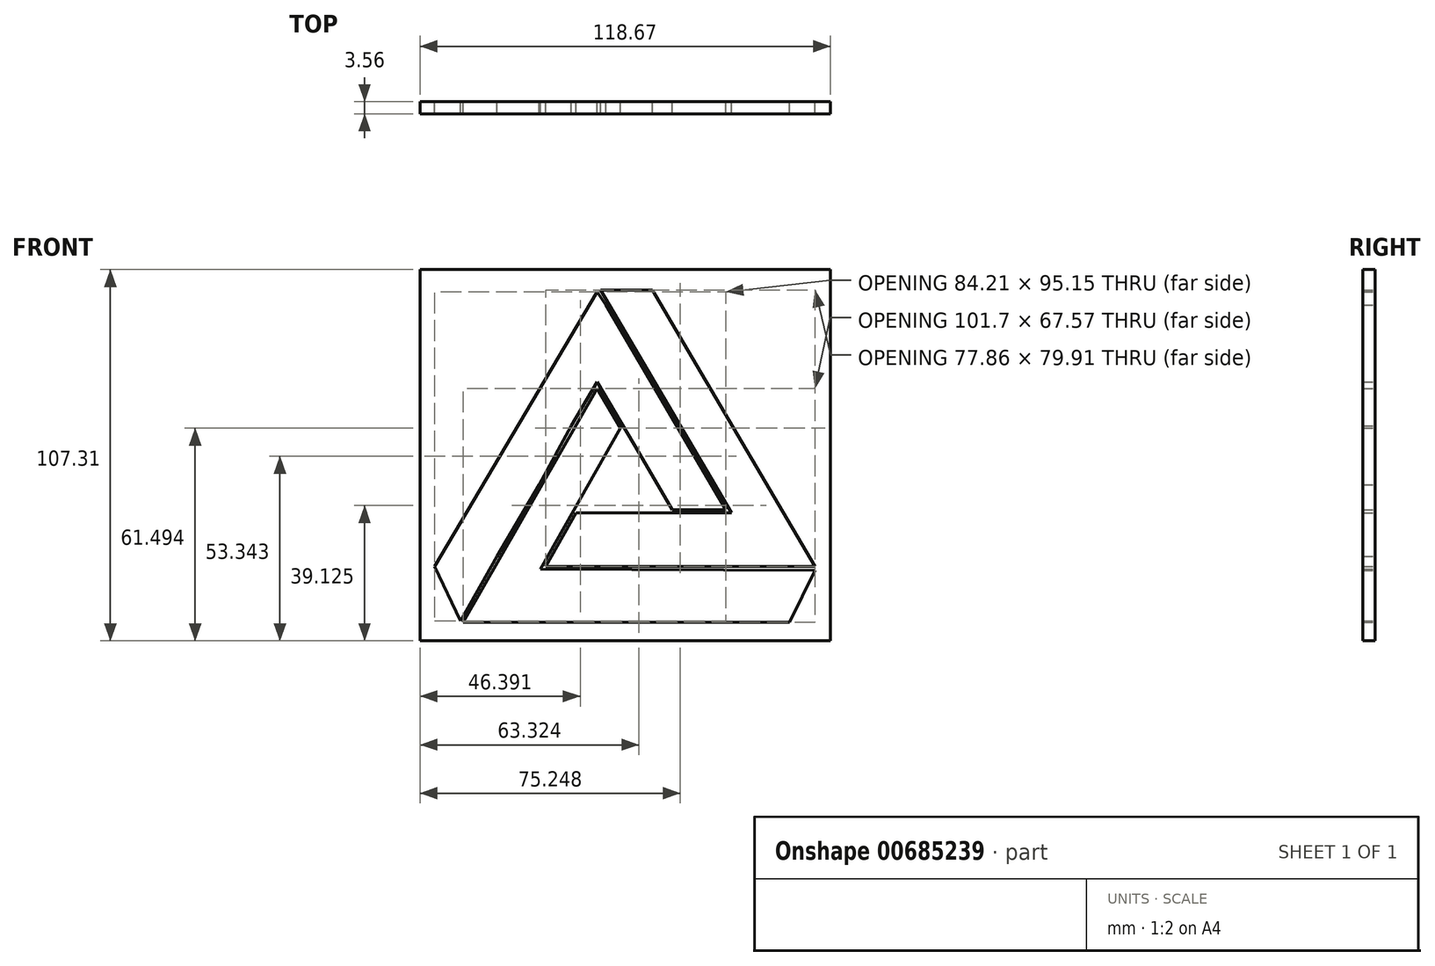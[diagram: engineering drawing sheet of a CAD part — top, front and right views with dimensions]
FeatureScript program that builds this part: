
annotation { "Feature Type Name" : "Feature", "Feature Type Description" : "" }
export const myFeature = defineFeature(function(context is Context, id is Id, definition is map)
    precondition{}
    {
        {
            var Q0;
            Q0=qCreatedBy(makeId("Front.planeOp"),FACE);
            var sketch = newSketch(context, id + "F0", { "sketchPlane" : qUnion([Q0])});
            skLineSegment(sketch, "E0", {"start": v(-4.74, 43.06) * mm, "end": v(10.26, 43.06) * mm});
            skLineSegment(sketch, "E1", {"start": v(10.26, 43.06) * mm, "end": v(19.28, 27.66) * mm});
            skLineSegment(sketch, "E2", {"start": v(19.28, 27.66) * mm, "end": v(57.2, -36.85) * mm});
            skLineSegment(sketch, "E3", {"start": v(57.2, -36.85) * mm, "end": v(22.98, -36.85) * mm});
            skLineSegment(sketch, "E4", {"start": v(22.98, -36.85) * mm, "end": v(-20.65, -36.85) * mm});
            skLineSegment(sketch, "E5", {"start": v(-20.65, -36.85) * mm, "end": v(-11.9, -21.44) * mm});
            skLineSegment(sketch, "E6", {"start": v(-11.9, -21.44) * mm, "end": v(33.16, -21.44) * mm});
            skLineSegment(sketch, "E7", {"start": v(33.16, -21.44) * mm, "end": v(-4.74, 43.06) * mm});
            skLineSegment(sketch, "E8", {"start": v(-5.76, 42.53) * mm, "end": v(-26.28, 7.81) * mm});
            skLineSegment(sketch, "E9", {"start": v(-26.28, 7.81) * mm, "end": v(-52.68, -36.85) * mm});
            skLineSegment(sketch, "E10", {"start": v(-52.68, -36.85) * mm, "end": v(-45.26, -52.62) * mm});
            skLineSegment(sketch, "E11", {"start": v(-45.26, -52.62) * mm, "end": v(-34.75, -33.95) * mm});
            skLineSegment(sketch, "E12", {"start": v(-34.75, -33.95) * mm, "end": v(-30.35, -26.51) * mm});
            skLineSegment(sketch, "E13", {"start": v(-30.35, -26.51) * mm, "end": v(-22.52, -13.27) * mm});
            skLineSegment(sketch, "E14", {"start": v(-22.52, -13.27) * mm, "end": v(-13.24, 3.73) * mm});
            skLineSegment(sketch, "E15", {"start": v(-13.24, 3.73) * mm, "end": v(-5.73, 16.44) * mm});
            skLineSegment(sketch, "E16", {"start": v(-5.73, 16.44) * mm, "end": v(6.53, -4.42) * mm});
            skLineSegment(sketch, "E17", {"start": v(6.53, -4.42) * mm, "end": v(15.97, -20.47) * mm});
            skLineSegment(sketch, "E18", {"start": v(15.97, -20.47) * mm, "end": v(31.52, -20.47) * mm});
            skLineSegment(sketch, "E19", {"start": v(31.52, -20.47) * mm, "end": v(23.42, -6.68) * mm});
            skLineSegment(sketch, "E20", {"start": v(23.42, -6.68) * mm, "end": v(16.9, 4.43) * mm});
            skLineSegment(sketch, "E21", {"start": v(16.9, 4.43) * mm, "end": v(12.07, 12.63) * mm});
            skLineSegment(sketch, "E22", {"start": v(12.07, 12.63) * mm, "end": v(5.95, 23.05) * mm});
            skLineSegment(sketch, "E23", {"start": v(5.95, 23.05) * mm, "end": v(-3.23, 38.67) * mm});
            skLineSegment(sketch, "E24", {"start": v(-3.23, 38.67) * mm, "end": v(-5.76, 42.53) * mm});
            skLineSegment(sketch, "E25", {"start": v(57.2, -37.99) * mm, "end": v(49.84, -53.05) * mm});
            skLineSegment(sketch, "E26", {"start": v(49.84, -53.05) * mm, "end": v(-44.5, -53.05) * mm});
            skLineSegment(sketch, "E27", {"start": v(-44.5, -53.05) * mm, "end": v(-5.76, 14.52) * mm});
            skLineSegment(sketch, "E28", {"start": v(-5.76, 14.52) * mm, "end": v(0.97, 3.08) * mm});
            skLineSegment(sketch, "E29", {"start": v(0.97, 3.08) * mm, "end": v(-22.15, -37.6) * mm});
            skLineSegment(sketch, "E30", {"start": v(-22.15, -37.6) * mm, "end": v(57.2, -37.99) * mm});
            skLineSegment(sketch, "E31.bottom", {"start": v(-56.97, 48.92) * mm, "end": v(61.7, 48.92) * mm});
            skLineSegment(sketch, "E31.top", {"start": v(-56.97, -58.39) * mm, "end": v(61.7, -58.39) * mm});
            skLineSegment(sketch, "E31.left", {"start": v(-56.97, 48.92) * mm, "end": v(-56.97, -58.39) * mm});
            skLineSegment(sketch, "E31.right", {"start": v(61.7, 48.92) * mm, "end": v(61.7, -58.39) * mm});
            skSolve(sketch);
        }
        {
            var Q0;
            Q0 = qSketchRegion(id + "F0", true);
            extrude(context, id + "F1", {"entities" : qUnion([Q0]), "depth" : 3.56 * mm, "offsetDistance" : 25.4 * mm});
        }
    });
